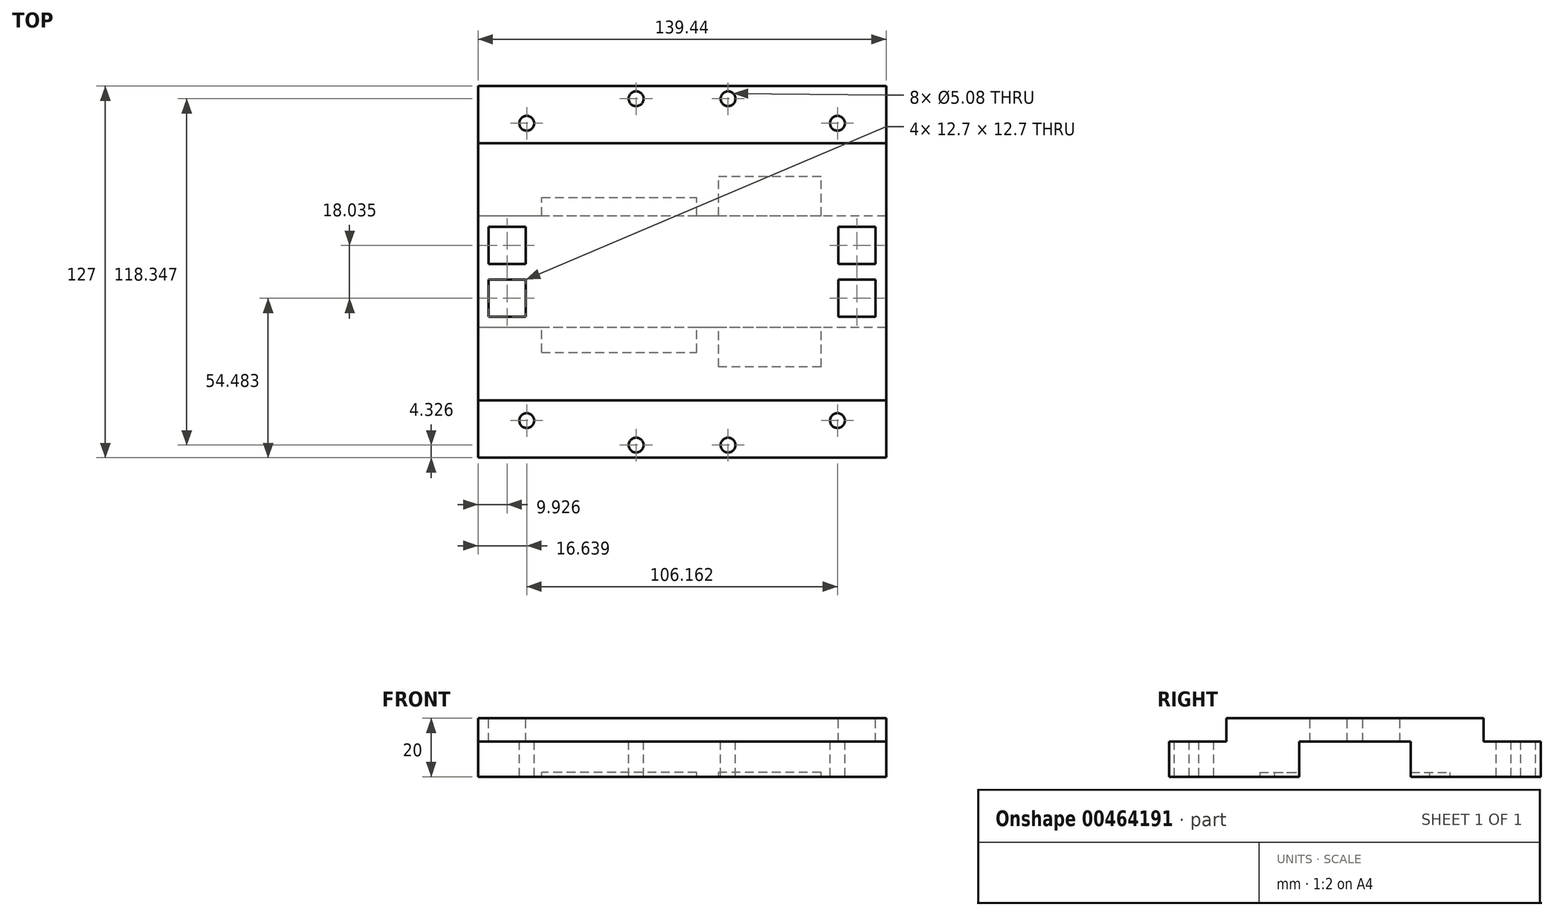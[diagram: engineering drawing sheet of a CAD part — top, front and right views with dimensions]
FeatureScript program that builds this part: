
annotation { "Feature Type Name" : "Feature", "Feature Type Description" : "" }
export const myFeature = defineFeature(function(context is Context, id is Id, definition is map)
    precondition{}
    {
        {
            var Q0;
            Q0=qCreatedBy(makeId("Front.planeOp"),FACE);
            var sketch = newSketch(context, id + "F0", { "sketchPlane" : qUnion([Q0])});
            skLineSegment(sketch, "E0.bottom", {"start": v(69.72, 10) * mm, "end": v(-69.72, 10) * mm});
            skLineSegment(sketch, "E0.top", {"start": v(69.72, -10) * mm, "end": v(-69.72, -10) * mm});
            skLineSegment(sketch, "E0.left", {"start": v(69.72, 10) * mm, "end": v(69.72, -10) * mm});
            skLineSegment(sketch, "E0.right", {"start": v(-69.72, 10) * mm, "end": v(-69.72, -10) * mm});
            skPoint(sketch, "E0.middle", {"position": v(0, 0) * mm});
            skSolve(sketch);
        }
        {
            var Q0;
            Q0=qSketchRegion(id+"F0",true);
            extrude(context, id + "F1", {"entities" : qUnion([Q0]), "endBound" : BoundingType.SYMMETRIC, "depth" : 127 * mm, "offsetDistance" : 25 * mm});
        }
        {
            var Q0;
            Q0=makeQuery(id+"F1.opExtrude","SWEPT_FACE",FACE,{"disambiguationData":[OSD([sQuery(id+"F0.wireOp",EDGE,"E0.bottom")])]});
            var sketch = newSketch(context, id + "F2", { "sketchPlane" : qUnion([Q0])});
            skLineSegment(sketch, "E1.bottom", {"start": v(-69.72, -63.5) * mm, "end": v(69.72, -63.5) * mm});
            skLineSegment(sketch, "E1.top", {"start": v(-69.72, -43.93) * mm, "end": v(69.72, -43.93) * mm});
            skLineSegment(sketch, "E1.left", {"start": v(-69.72, -63.5) * mm, "end": v(-69.72, -43.93) * mm});
            skLineSegment(sketch, "E1.right", {"start": v(69.72, -63.5) * mm, "end": v(69.72, -43.93) * mm});
            skSolve(sketch);
        }
        {
            var Q0;
            Q0=makeQuery(id+"F2.imprint","IMPRINT",FACE,{"disambiguationData":[TD([[makeQuery(id+"F2.imprint","IMPRINT",EDGE,{"derivedFrom":sQuery(id+"F2.wireOp",EDGE,"E1.bottom")}),-1.0]])]});
            extrude(context, id + "F3", {"entities" : qUnion([Q0]), "operationType" : NewBodyOperationType.REMOVE, "oppositeDirection" : true, "depth" : 8 * mm});
        }
        {
            var Q0;
            Q0=makeQuery(id+"F1.opExtrude","SWEPT_BODY",BODY,{"disambiguationData":[OSD([sQuery(id+"F0.wireOp",EDGE,"E0.bottom"),sQuery(id+"F0.wireOp",EDGE,"E0.top"),sQuery(id+"F0.wireOp",EDGE,"E0.left"),sQuery(id+"F0.wireOp",EDGE,"E0.right")])]});
            var Q1;
            Q1=qCreatedBy(makeId("Front.planeOp"),FACE);
            mirror(context, id + "F4", {"operationType" : NewBodyOperationType.INTERSECT, "entities" : qUnion([Q0]), "mirrorPlane" : qUnion([Q1])});
        }
        {
            var Q0;
            Q0=makeQuery(id+"F1.opExtrude","SWEPT_FACE",FACE,{"disambiguationData":[OSD([sQuery(id+"F0.wireOp",EDGE,"E0.bottom")])]});
            var sketch = newSketch(context, id + "F5", { "sketchPlane" : qUnion([Q0])});
            skLineSegment(sketch, "E2.bottom", {"start": v(66.14, -15.37) * mm, "end": v(53.44, -15.37) * mm});
            skLineSegment(sketch, "E2.top", {"start": v(66.14, -2.67) * mm, "end": v(53.44, -2.67) * mm});
            skLineSegment(sketch, "E2.left", {"start": v(66.14, -15.37) * mm, "end": v(66.14, -2.67) * mm});
            skLineSegment(sketch, "E2.right", {"start": v(53.44, -15.37) * mm, "end": v(53.44, -2.67) * mm});
            skSolve(sketch);
        }
        {
            var Q0;
            Q0=makeQuery(id+"F5.imprint","IMPRINT",FACE,{"disambiguationData":[TD([[makeQuery(id+"F5.imprint","IMPRINT",EDGE,{"derivedFrom":sQuery(id+"F5.wireOp",EDGE,"E2.bottom")}),-1.0]])]});
            extrude(context, id + "F6", {"entities" : qUnion([Q0]), "operationType" : NewBodyOperationType.REMOVE, "oppositeDirection" : true, "depth" : 21.84 * mm});
        }
        {
            var Q0;
            Q0=qCreatedBy(makeId("Top.planeOp"),FACE);
            var sketch = newSketch(context, id + "F7", { "sketchPlane" : qUnion([Q0])});
            skLineSegment(sketch, "E3.bottom", {"start": v(47.75, 29.72) * mm, "end": v(-47.75, 29.72) * mm});
            skLineSegment(sketch, "E3.top", {"start": v(47.75, -29.72) * mm, "end": v(-47.75, -29.72) * mm});
            skLineSegment(sketch, "E3.left", {"start": v(47.75, 29.72) * mm, "end": v(47.75, -29.72) * mm});
            skLineSegment(sketch, "E3.right", {"start": v(-47.75, 29.72) * mm, "end": v(-47.75, -29.72) * mm});
            skPoint(sketch, "E3.middle", {"position": v(0, 0) * mm});
            skSolve(sketch);
        }
        {
            var Q0;
            Q0=makeQuery(id+"F3.boolean.opBoolean","COPY",FACE,{"derivedFrom":makeQuery(id+"F3.opExtrude","CAP_FACE",FACE,{"disambiguationData":[OSD([sQuery(id+"F2.wireOp",EDGE,"E1.bottom"),sQuery(id+"F2.wireOp",EDGE,"E1.top"),sQuery(id+"F2.wireOp",EDGE,"E1.left"),sQuery(id+"F2.wireOp",EDGE,"E1.right")])],"isStart":false})});
            var sketch = newSketch(context, id + "F8", { "sketchPlane" : qUnion([Q0])});
            skPoint(sketch, "E4.middle", {"position": v(0, 0) * mm});
            skCircle(sketch, "E5", {"center": v(53.08, -50.8) * mm, "radius": 2.54 * mm});
            skCircle(sketch, "E6", {"center": v(15.7, -59.17) * mm, "radius": 2.54 * mm});
            skSolve(sketch);
        }
        {
            var Q0;
            Q0=qSketchRegion(id+"F8",true);
            extrude(context, id + "F9", {"entities" : qUnion([Q0]), "operationType" : NewBodyOperationType.REMOVE, "oppositeDirection" : true, "depth" : 76.2 * mm, "offsetDistance" : 25 * mm});
        }
        {
            var Q0;
            Q0=makeQuery(id+"F1.opExtrude","SWEPT_BODY",BODY,{"disambiguationData":[OSD([sQuery(id+"F0.wireOp",EDGE,"E0.bottom"),sQuery(id+"F0.wireOp",EDGE,"E0.top"),sQuery(id+"F0.wireOp",EDGE,"E0.left"),sQuery(id+"F0.wireOp",EDGE,"E0.right")])]});
            var Q1;
            Q1=qCreatedBy(makeId("Front.planeOp"),FACE);
            mirror(context, id + "F10", {"operationType" : NewBodyOperationType.INTERSECT, "entities" : qUnion([Q0]), "mirrorPlane" : qUnion([Q1])});
        }
        {
            var Q0;
            Q0=makeQuery(id+"F1.opExtrude","SWEPT_BODY",BODY,{"disambiguationData":[OSD([sQuery(id+"F0.wireOp",EDGE,"E0.bottom"),sQuery(id+"F0.wireOp",EDGE,"E0.top"),sQuery(id+"F0.wireOp",EDGE,"E0.left"),sQuery(id+"F0.wireOp",EDGE,"E0.right")])]});
            var Q1;
            Q1=qCreatedBy(makeId("Right.planeOp"),FACE);
            mirror(context, id + "F11", {"operationType" : NewBodyOperationType.INTERSECT, "entities" : qUnion([Q0]), "mirrorPlane" : qUnion([Q1])});
        }
        {
            var Q0;
            Q0=makeQuery(id+"F1.opExtrude","SWEPT_FACE",FACE,{"disambiguationData":[OSD([sQuery(id+"F0.wireOp",EDGE,"E0.top")])]});
            var sketch = newSketch(context, id + "F12", { "sketchPlane" : qUnion([Q0])});
            skPoint(sketch, "E7", {"position": v(0, 0) * mm});
            skLineSegment(sketch, "E8.bottom", {"start": v(69.72, 18.98) * mm, "end": v(1.72, 18.98) * mm});
            skLineSegment(sketch, "E8.top", {"start": v(69.72, -19.12) * mm, "end": v(1.72, -19.12) * mm});
            skLineSegment(sketch, "E8.left", {"start": v(69.72, 18.98) * mm, "end": v(69.72, -19.12) * mm});
            skLineSegment(sketch, "E9", {"start": v(1.72, 18.98) * mm, "end": v(-69.72, 18.98) * mm});
            skLineSegment(sketch, "E10", {"start": v(1.72, -19.12) * mm, "end": v(-69.72, -19.12) * mm});
            skLineSegment(sketch, "E11", {"start": v(-69.72, -19.12) * mm, "end": v(-69.72, 18.98) * mm});
            skPoint(sketch, "E12.oppositeSnap0", {"position": v(59.8, 15.37) * mm});
            skPoint(sketch, "E13.oppositeSnap0", {"position": v(59.8, -15.37) * mm});
            skPoint(sketch, "E14.oppositeSnap0", {"position": v(-59.8, -15.37) * mm});
            skPoint(sketch, "E15.oppositeSnap0", {"position": v(-59.8, 15.37) * mm});
            skSolve(sketch);
        }
        {
            var Q0;
            Q0=makeQuery(id+"F1.opExtrude","SWEPT_FACE",FACE,{"disambiguationData":[OSD([sQuery(id+"F0.wireOp",EDGE,"E0.top")])]});
            var sketch = newSketch(context, id + "F13", { "sketchPlane" : qUnion([Q0])});
            skPoint(sketch, "E16.middle", {"position": v(0, 0) * mm});
            skLineSegment(sketch, "E17.bottom", {"start": v(-48.01, 27.5) * mm, "end": v(4.99, 27.5) * mm});
            skLineSegment(sketch, "E17.top", {"start": v(-48.01, -25.5) * mm, "end": v(4.99, -25.5) * mm});
            skLineSegment(sketch, "E17.left", {"start": v(-48.01, 27.5) * mm, "end": v(-48.01, -25.5) * mm});
            skLineSegment(sketch, "E17.right", {"start": v(4.99, 27.5) * mm, "end": v(4.99, -25.5) * mm});
            skPoint(sketch, "E17.middle", {"position": v(-21.51, 1) * mm});
            skPoint(sketch, "E17.middle.positionSnap0", {"position": v(-24.5, 1) * mm});
            skPoint(sketch, "E17.centerSnap0", {"position": v(-24.5, 1) * mm});
            skLineSegment(sketch, "E18.bottom", {"start": v(47.5, 32.5) * mm, "end": v(12.5, 32.5) * mm});
            skLineSegment(sketch, "E18.top", {"start": v(47.5, -32.5) * mm, "end": v(12.5, -32.5) * mm});
            skLineSegment(sketch, "E18.left", {"start": v(47.5, 32.5) * mm, "end": v(47.5, -32.5) * mm});
            skLineSegment(sketch, "E18.right", {"start": v(12.5, 32.5) * mm, "end": v(12.5, -32.5) * mm});
            skPoint(sketch, "E18.middle", {"position": v(30, 0) * mm});
            skSolve(sketch);
        }
        {
            var Q0;
            Q0=qSketchRegion(id+"F13",true);
            extrude(context, id + "F14", {"entities" : qUnion([Q0]), "operationType" : NewBodyOperationType.REMOVE, "oppositeDirection" : true, "depth" : 1.5 * mm, "offsetDistance" : 25 * mm});
        }
        {
            var Q0;
            Q0=qSketchRegion(id+"F12",true);
            extrude(context, id + "F15", {"entities" : qUnion([Q0]), "operationType" : NewBodyOperationType.REMOVE, "oppositeDirection" : true, "depth" : 12 * mm, "offsetDistance" : 25 * mm});
        }
    });
